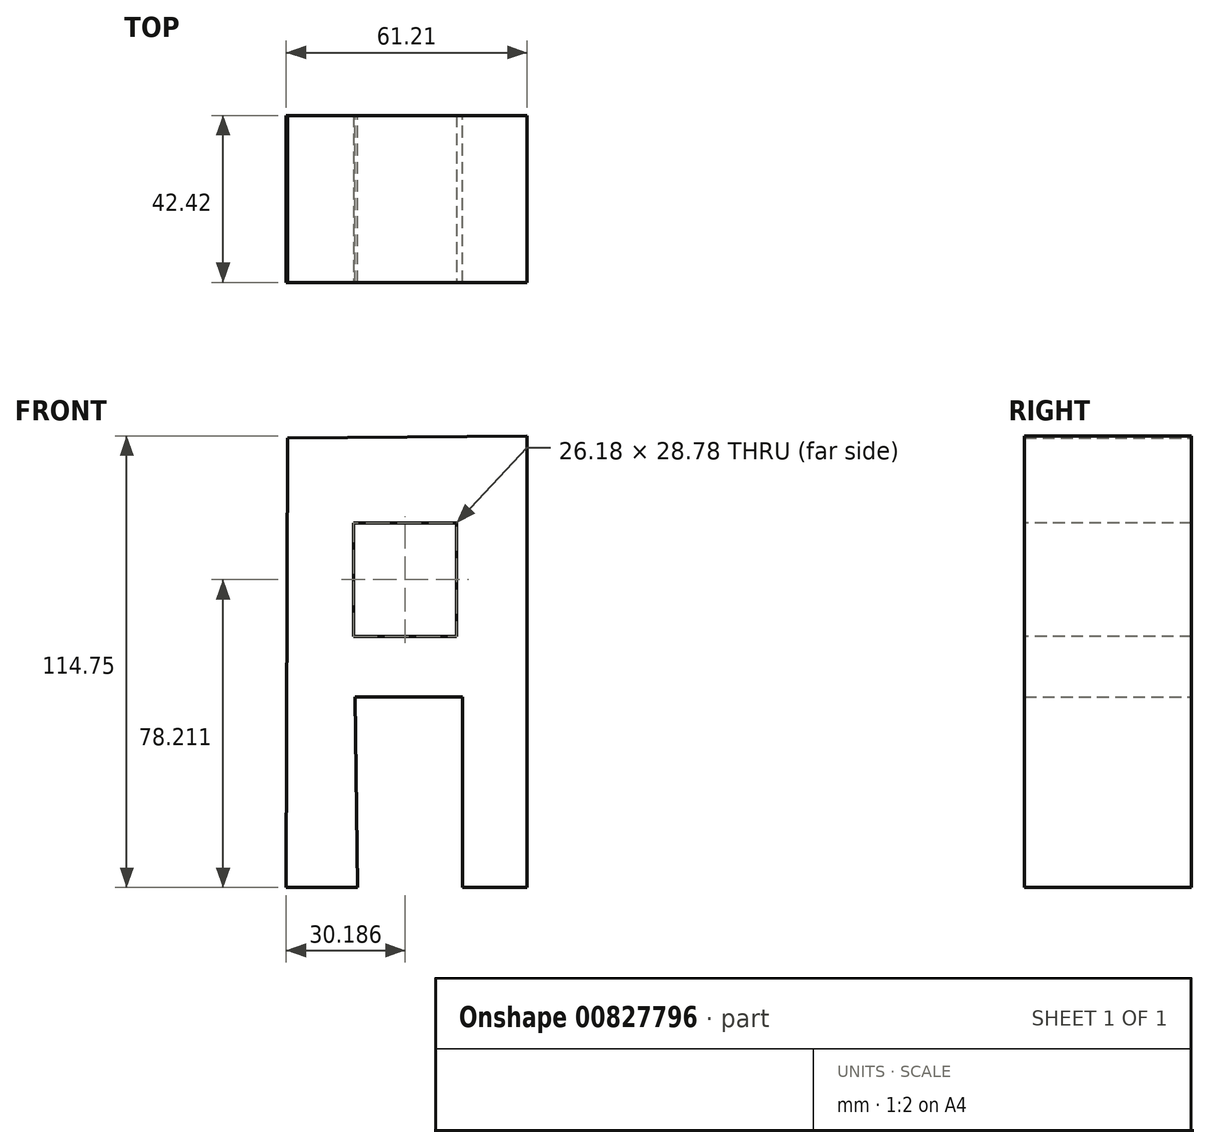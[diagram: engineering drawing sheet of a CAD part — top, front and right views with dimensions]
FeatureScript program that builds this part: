
annotation { "Feature Type Name" : "Feature", "Feature Type Description" : "" }
export const myFeature = defineFeature(function(context is Context, id is Id, definition is map)
    precondition{}
    {
        {
            var Q0;
            Q0=qCreatedBy(makeId("Front.planeOp"),FACE);
            var sketch = newSketch(context, id + "F0", { "sketchPlane" : qUnion([Q0])});
            skLineSegment(sketch, "E0", {"start": v(-93.45, 50.37) * mm, "end": v(-93.86, -63.82) * mm});
            skLineSegment(sketch, "E1", {"start": v(-93.86, -63.82) * mm, "end": v(-75.77, -63.82) * mm});
            skLineSegment(sketch, "E2", {"start": v(-75.77, -63.82) * mm, "end": v(-76.4, -15.35) * mm});
            skLineSegment(sketch, "E3", {"start": v(-76.4, -15.35) * mm, "end": v(-49.03, -15.35) * mm});
            skLineSegment(sketch, "E4", {"start": v(-49.03, -15.35) * mm, "end": v(-49.03, -63.82) * mm});
            skLineSegment(sketch, "E5", {"start": v(-49.03, -63.82) * mm, "end": v(-32.65, -63.82) * mm});
            skLineSegment(sketch, "E6", {"start": v(-32.65, -63.82) * mm, "end": v(-32.65, 50.93) * mm});
            skLineSegment(sketch, "E7", {"start": v(-32.65, 50.93) * mm, "end": v(-93.45, 50.37) * mm});
            skPoint(sketch, "E8", {"position": v(-97.4, -8.53) * mm});
            skSolve(sketch);
        }
        {
            var Q0;
            Q0=makeQuery(id+"F0.imprint","IMPRINT",FACE,{"disambiguationData":[TD([[makeQuery(id+"F0.imprint","IMPRINT",EDGE,{"derivedFrom":sQuery(id+"F0.wireOp",EDGE,"E0")}),1.0]])]});
            extrude(context, id + "F1", {"entities" : qUnion([Q0]), "depth" : 42.42 * mm, "offsetDistance" : 25.4 * mm});
        }
        {
            var Q0;
            Q0=makeQuery(id+"F1.opExtrude","CAP_FACE",FACE,{"disambiguationData":[OSD([sQuery(id+"F0.wireOp",EDGE,"E0"),sQuery(id+"F0.wireOp",EDGE,"E1"),sQuery(id+"F0.wireOp",EDGE,"E2"),sQuery(id+"F0.wireOp",EDGE,"E3"),sQuery(id+"F0.wireOp",EDGE,"E4"),sQuery(id+"F0.wireOp",EDGE,"E5"),sQuery(id+"F0.wireOp",EDGE,"E6"),sQuery(id+"F0.wireOp",EDGE,"E7")])],"isStart":false});
            var sketch = newSketch(context, id + "F2", { "sketchPlane" : qUnion([Q0])});
            skLineSegment(sketch, "E9.bottom", {"start": v(-50.59, 0) * mm, "end": v(-76.76, 0) * mm});
            skLineSegment(sketch, "E9.top", {"start": v(-50.59, 28.78) * mm, "end": v(-76.76, 28.78) * mm});
            skLineSegment(sketch, "E9.left", {"start": v(-50.59, 0) * mm, "end": v(-50.59, 28.78) * mm});
            skLineSegment(sketch, "E9.right", {"start": v(-76.76, 0) * mm, "end": v(-76.76, 28.78) * mm});
            skPoint(sketch, "E9.middle", {"position": v(-63.67, 14.4) * mm});
            skSolve(sketch);
        }
        {
            var Q0;
            Q0=makeQuery(id+"F2.imprint","IMPRINT",FACE,{"disambiguationData":[TD([[makeQuery(id+"F2.imprint","IMPRINT",EDGE,{"derivedFrom":sQuery(id+"F2.wireOp",EDGE,"E9.bottom")}),-1.0]])]});
            extrude(context, id + "F3", {"entities" : qUnion([Q0]), "operationType" : NewBodyOperationType.REMOVE, "oppositeDirection" : true, "depth" : 108.97 * mm, "offsetDistance" : 25.4 * mm});
        }
    });
